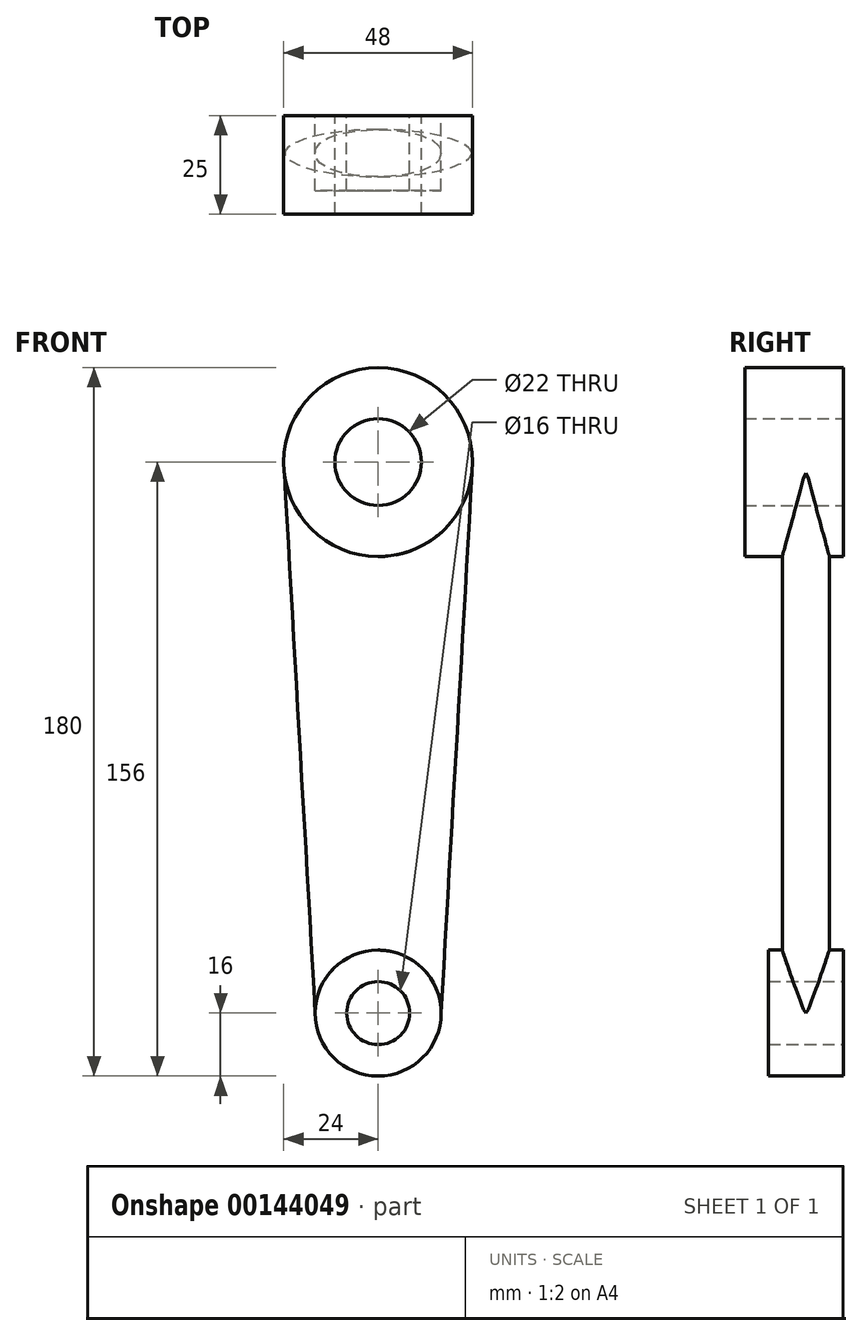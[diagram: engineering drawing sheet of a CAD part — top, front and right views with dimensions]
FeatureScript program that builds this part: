
annotation { "Feature Type Name" : "Feature", "Feature Type Description" : "" }
export const myFeature = defineFeature(function(context is Context, id is Id, definition is map)
    precondition{}
    {
        {
            var Q0;
            Q0=qCreatedBy(makeId("Front.planeOp"),FACE);
            var sketch = newSketch(context, id + "F0", { "sketchPlane" : qUnion([Q0])});
            skCircle(sketch, "E0", {"center": v(0, 0) * mm, "radius": 8 * mm});
            skCircle(sketch, "E1", {"center": v(0, 0) * mm, "radius": 16 * mm});
            skCircle(sketch, "E2", {"center": v(0, 140) * mm, "radius": 11 * mm});
            skCircle(sketch, "E3", {"center": v(0, 140) * mm, "radius": 24 * mm});
            skSolve(sketch);
        }
        {
            var Q0;
            Q0=makeQuery(id+"F0.imprint","IMPRINT",FACE,{"disambiguationData":[TD([[makeQuery(id+"F0.imprint","IMPRINT",EDGE,{"derivedFrom":sQuery(id+"F0.wireOp",EDGE,"E0")}),-1.0]])]});
            var Q1;
            Q1=makeQuery(id+"F0.imprint","IMPRINT",FACE,{"disambiguationData":[TD([[makeQuery(id+"F0.imprint","IMPRINT",EDGE,{"derivedFrom":sQuery(id+"F0.wireOp",EDGE,"E0")}),1.0]])]});
            extrude(context, id + "F1", {"entities" : qUnion([Q0, Q1]), "depth" : 19 * mm});
        }
        {
            var Q0;
            Q0=makeQuery(id+"F0.imprint","IMPRINT",FACE,{"disambiguationData":[TD([[makeQuery(id+"F0.imprint","IMPRINT",EDGE,{"derivedFrom":sQuery(id+"F0.wireOp",EDGE,"E2")}),-1.0]])]});
            var Q1;
            Q1=makeQuery(id+"F0.imprint","IMPRINT",FACE,{"disambiguationData":[TD([[makeQuery(id+"F0.imprint","IMPRINT",EDGE,{"derivedFrom":sQuery(id+"F0.wireOp",EDGE,"E2")}),1.0]])]});
            extrude(context, id + "F2", {"entities" : qUnion([Q0, Q1]), "depth" : 25 * mm});
        }
        {
            var Q0;
            Q0=qCreatedBy(makeId("Top.planeOp"),FACE);
            var sketch = newSketch(context, id + "F3", { "sketchPlane" : qUnion([Q0])});
            skEllipse(sketch, "E4", {"center": v(0, -9.5) * mm, "majorRadius": 16 * mm, "minorRadius": 6 * mm, "majorAxis": v(1, 0)});
            skPoint(sketch, "E5", {"position": v(0, -3.5) * mm});
            skLineSegment(sketch, "E6", {"start": v(0, 0) * mm, "end": v(16, 0) * mm, "construction": true});
            skLineSegment(sketch, "E7", {"start": v(16, 0) * mm, "end": v(16, -18.74) * mm, "construction": true});
            skSolve(sketch);
        }
        {
            var Q0;
            Q0=sQuery(id+"F0.wireOp",VERTEX,"E3.center");
            var Q1;
            Q1=qCreatedBy(makeId("Top.planeOp"),FACE);
            cPlane(context, id + "F4", {"entities" : qUnion([Q0, Q1]), "cplaneType" : CPlaneType.PLANE_POINT, "offset" : 25 * mm, "width" : 150 * mm, "height" : 150 * mm});
        }
        {
            var Q0;
            Q0=qCreatedBy(id+"F4.planeOp",FACE);
            var sketch = newSketch(context, id + "F5", { "sketchPlane" : qUnion([Q0])});
            skEllipse(sketch, "E8", {"center": v(0, -9.5) * mm, "majorRadius": 24 * mm, "minorRadius": 6 * mm, "majorAxis": v(1, 0)});
            skPoint(sketch, "E9", {"position": v(0, -3.5) * mm});
            skLineSegment(sketch, "E10", {"start": v(0, 0) * mm, "end": v(24, 0) * mm, "construction": true});
            skLineSegment(sketch, "E11", {"start": v(24, 0) * mm, "end": v(24, -24.8) * mm, "construction": true});
            skSolve(sketch);
        }
        {
            var Q0;
            Q0=makeQuery(id+"F5.imprint","IMPRINT",FACE,{"disambiguationData":[TD([[makeQuery(id+"F5.imprint","IMPRINT",EDGE,{"derivedFrom":sQuery(id+"F5.wireOp",EDGE,"E8")}),1.0]])]});
            var Q1;
            Q1=makeQuery(id+"F3.imprint","IMPRINT",FACE,{"disambiguationData":[TD([[makeQuery(id+"F3.imprint","IMPRINT",EDGE,{"derivedFrom":sQuery(id+"F3.wireOp",EDGE,"E4")}),1.0]])]});
            loft(context, id + "F6", {"operationType" : NewBodyOperationType.ADD, "sheetProfilesArray" : [{ "sheetProfileEntities" : qUnion([Q0]) }, { "sheetProfileEntities" : qUnion([Q1]) }]});
        }
        {
            var Q0;
            Q0=makeQuery(id+"F0.imprint","IMPRINT",FACE,{"disambiguationData":[TD([[makeQuery(id+"F0.imprint","IMPRINT",EDGE,{"derivedFrom":sQuery(id+"F0.wireOp",EDGE,"E2")}),1.0]])]});
            var Q1;
            Q1=makeQuery(id+"F0.imprint","IMPRINT",FACE,{"disambiguationData":[TD([[makeQuery(id+"F0.imprint","IMPRINT",EDGE,{"derivedFrom":sQuery(id+"F0.wireOp",EDGE,"E0")}),1.0]])]});
            extrude(context, id + "F7", {"entities" : qUnion([Q0, Q1]), "operationType" : NewBodyOperationType.REMOVE, "endBound" : BoundingType.THROUGH_ALL, "depth" : 25 * mm});
        }
    });
